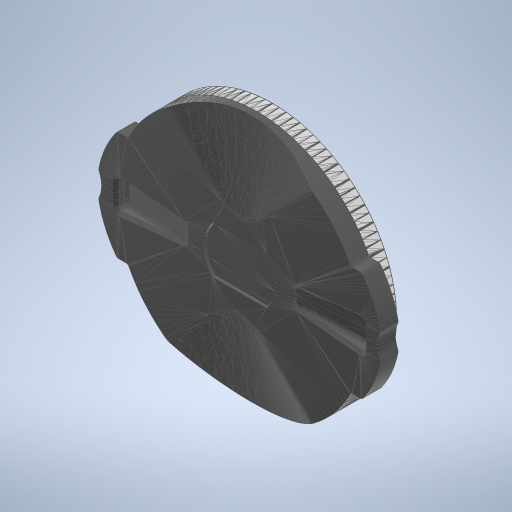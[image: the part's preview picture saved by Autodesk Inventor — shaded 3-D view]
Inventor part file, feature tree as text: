
AUTODESK INVENTOR PART (.ipt)
format: ipt  version: 2023 (Build 270158000, 158)  size: 352,768 bytes
history: native  units: in
note: dims shown in document units (in); Inventor stores cm internally (conversion verified against a paired STEP export)
features: other x2, plane x1, extrude x1, sketch x1
ambient origin geometry x8: Origin, YZ Plane, XZ Plane, XY Plane, X Axis, Y Axis, Z Axis, Center Point
bodies: Solid1 (feature_tree)
feature tree (5):
  other  "GarminQuarterTurn"
  plane  "Work Plane2"
  extrude  "Extrusion1"  [1 undecoded]
  sketch  "Sketch2"  dims[d1=1.5in d2=0.0in]
  other  "MeshFeature1"
note: 1 required parameter value undecoded (feature->parameter linkage not recoverable at this tier; creation-order binding heuristic only, values carry confidence <= 0.55)
